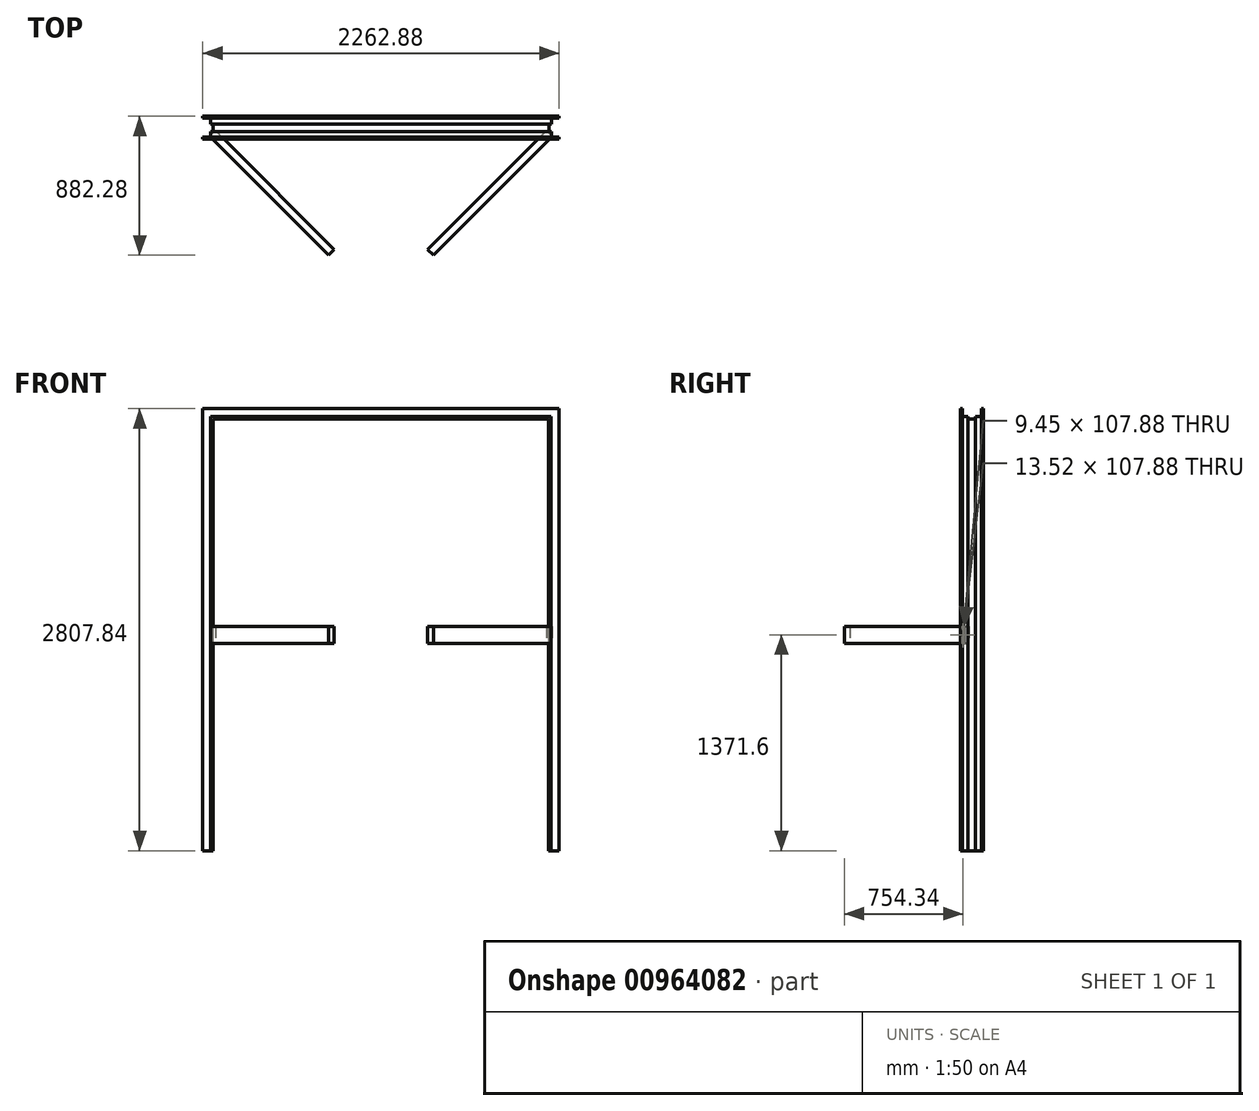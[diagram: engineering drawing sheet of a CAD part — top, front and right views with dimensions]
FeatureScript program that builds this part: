
annotation { "Feature Type Name" : "Feature", "Feature Type Description" : "" }
export const myFeature = defineFeature(function(context is Context, id is Id, definition is map)
    precondition{}
    {
        {
            assignVariable(context, id + "F0", {"name" : "Length", "anyValue" : 108});
        }
        {
            var Q0;
            Q0=qCreatedBy(makeId("Front.planeOp"),FACE);
            var sketch = newSketch(context, id + "F1", { "sketchPlane" : qUnion([Q0])});
            skLineSegment(sketch, "E0.bottom", {"start": v(1066.8, -1371.6) * mm, "end": v(-1066.8, -1371.6) * mm});
            skLineSegment(sketch, "E0.top", {"start": v(1066.8, 1371.6) * mm, "end": v(-1066.8, 1371.6) * mm});
            skLineSegment(sketch, "E0.left", {"start": v(1066.8, -1371.6) * mm, "end": v(1066.8, 1371.6) * mm});
            skLineSegment(sketch, "E0.right", {"start": v(-1066.8, -1371.6) * mm, "end": v(-1066.8, 1371.6) * mm});
            skPoint(sketch, "E0.middle", {"position": v(0, 0) * mm});
            skSolve(sketch);
        }
        {
            var Q0;
            Q0=qCreatedBy(makeId("Top.planeOp"),FACE);
            var sketch = newSketch(context, id + "F2", { "sketchPlane" : qUnion([Q0])});
            skLineSegment(sketch, "E1", {"start": v(-1066.8, 23.37) * mm, "end": v(-1066.8, -23.37) * mm});
            skLineSegment(sketch, "E2", {"start": v(-1066.8, -23.37) * mm, "end": v(-1082.68, -23.37) * mm});
            skLineSegment(sketch, "E3", {"start": v(-1082.68, -23.37) * mm, "end": v(-1082.68, -71) * mm});
            skLineSegment(sketch, "E4", {"start": v(-1082.68, -71) * mm, "end": v(-1129.41, -71) * mm});
            skLineSegment(sketch, "E5", {"start": v(-1129.41, -71) * mm, "end": v(-1129.41, -60.33) * mm});
            skLineSegment(sketch, "E6", {"start": v(-1066.8, 0) * mm, "end": v(-1067.42, 0) * mm, "construction": true});
            skLineSegment(sketch, "E7.MirrorCS", {"start": v(-1066.8, 23.37) * mm, "end": v(-1082.68, 23.37) * mm});
            skLineSegment(sketch, "E8.MirrorCS", {"start": v(-1082.68, 23.37) * mm, "end": v(-1082.68, 71) * mm});
            skLineSegment(sketch, "E9.MirrorCS", {"start": v(-1082.68, 71) * mm, "end": v(-1129.41, 71) * mm});
            skLineSegment(sketch, "E10.MirrorCS", {"start": v(-1129.41, 71) * mm, "end": v(-1129.41, 60.33) * mm});
            skLineSegment(sketch, "E11.MirrorCS", {"start": v(-1066.8, -23.37) * mm, "end": v(-1066.8, 23.37) * mm});
            skLineSegment(sketch, "E12.0", {"start": v(-1131.44, 73.02) * mm, "end": v(-1131.44, 60.33) * mm});
            skLineSegment(sketch, "E12.1", {"start": v(-1080.64, 73.03) * mm, "end": v(-1131.44, 73.02) * mm});
            skLineSegment(sketch, "E12.2", {"start": v(-1080.64, 25.4) * mm, "end": v(-1080.64, 73.03) * mm});
            skLineSegment(sketch, "E12.3", {"start": v(-1064.77, 25.4) * mm, "end": v(-1080.64, 25.4) * mm});
            skLineSegment(sketch, "E12.4", {"start": v(-1064.77, -25.4) * mm, "end": v(-1064.77, 25.4) * mm});
            skLineSegment(sketch, "E12.5", {"start": v(-1131.44, -73.03) * mm, "end": v(-1131.44, -60.33) * mm});
            skLineSegment(sketch, "E12.6", {"start": v(-1080.64, -73.03) * mm, "end": v(-1131.44, -73.03) * mm});
            skLineSegment(sketch, "E12.7", {"start": v(-1080.64, -25.4) * mm, "end": v(-1080.64, -73.03) * mm});
            skLineSegment(sketch, "E12.8", {"start": v(-1064.77, -25.4) * mm, "end": v(-1080.64, -25.4) * mm});
            skLineSegment(sketch, "E13", {"start": v(-1131.44, 60.33) * mm, "end": v(-1129.41, 60.33) * mm});
            skLineSegment(sketch, "E14", {"start": v(-1131.44, -60.33) * mm, "end": v(-1129.41, -60.33) * mm});
            skSolve(sketch);
        }
        {
            var Q0;
            Q0=qSketchRegion(id+"F2",true);
            var Q1;
            Q1=sQuery(id+"F1.wireOp",EDGE,"E0.right");
            var Q2;
            Q2=sQuery(id+"F1.wireOp",EDGE,"E0.top");
            var Q3;
            Q3=sQuery(id+"F1.wireOp",EDGE,"E0.left");
            sweep(context, id + "F3", {"profiles" : qUnion([Q0]), "path" : qUnion([Q1, Q2, Q3])});
        }
        {
            var Q0;
            Q0=qCreatedBy(makeId("Top.planeOp"),FACE);
            var sketch = newSketch(context, id + "F4", { "sketchPlane" : qUnion([Q0])});
            skLineSegment(sketch, "E15", {"start": v(-1051.48, -18.99) * mm, "end": v(-297.14, -773.33) * mm});
            skLineSegment(sketch, "E16", {"start": v(-297.14, -773.33) * mm, "end": v(-333.06, -809.25) * mm});
            skLineSegment(sketch, "E17", {"start": v(-333.06, -809.25) * mm, "end": v(-1087.4, -54.9) * mm});
            skLineSegment(sketch, "E18", {"start": v(-1087.4, -54.9) * mm, "end": v(-1051.48, -18.99) * mm});
            skSolve(sketch);
        }
        {
            var Q0;
            Q0=makeQuery(id+"F4.imprint","IMPRINT",FACE,{"disambiguationData":[TD([[makeQuery(id+"F4.imprint","IMPRINT",EDGE,{"derivedFrom":sQuery(id+"F4.wireOp",EDGE,"E15")}),-1.0]])]});
            extrude(context, id + "F5", {"entities" : qUnion([Q0]), "operationType" : NewBodyOperationType.ADD, "endBound" : BoundingType.SYMMETRIC, "depth" : (getVariable(context, 'Length') - .125) * mm, "offsetDistance" : 25.4 * mm});
        }
        {
            var Q0;
            Q0=makeQuery(id+"F3.opSweep","SWEPT_BODY",BODY,{"disambiguationData":[OSD([sQuery(id+"F1.wireOp",EDGE,"E0.left"),sQuery(id+"F2.wireOp",EDGE,"E7.MirrorCS"),sQuery(id+"F2.wireOp",EDGE,"E10.MirrorCS"),sQuery(id+"F2.wireOp",EDGE,"E9.MirrorCS"),sQuery(id+"F2.wireOp",EDGE,"E3"),sQuery(id+"F2.wireOp",EDGE,"E8.MirrorCS"),sQuery(id+"F2.wireOp",EDGE,"E2"),sQuery(id+"F2.wireOp",EDGE,"E11.MirrorCS"),sQuery(id+"F2.wireOp",EDGE,"E5"),sQuery(id+"F2.wireOp",EDGE,"E4"),sQuery(id+"F2.wireOp",EDGE,"E12.0"),sQuery(id+"F2.wireOp",EDGE,"E12.1"),sQuery(id+"F2.wireOp",EDGE,"E12.2"),sQuery(id+"F2.wireOp",EDGE,"E12.3"),sQuery(id+"F2.wireOp",EDGE,"E12.4"),sQuery(id+"F2.wireOp",EDGE,"E12.5"),sQuery(id+"F2.wireOp",EDGE,"E12.6"),sQuery(id+"F2.wireOp",EDGE,"E12.7"),sQuery(id+"F2.wireOp",EDGE,"E12.8"),sQuery(id+"F2.wireOp",EDGE,"E13"),sQuery(id+"F2.wireOp",EDGE,"E14")])]});
            var Q1;
            Q1=qCreatedBy(makeId("Right.planeOp"),FACE);
            mirror(context, id + "F6", {"operationType" : NewBodyOperationType.ADD, "entities" : qUnion([Q0]), "mirrorPlane" : qUnion([Q1])});
        }
    });
